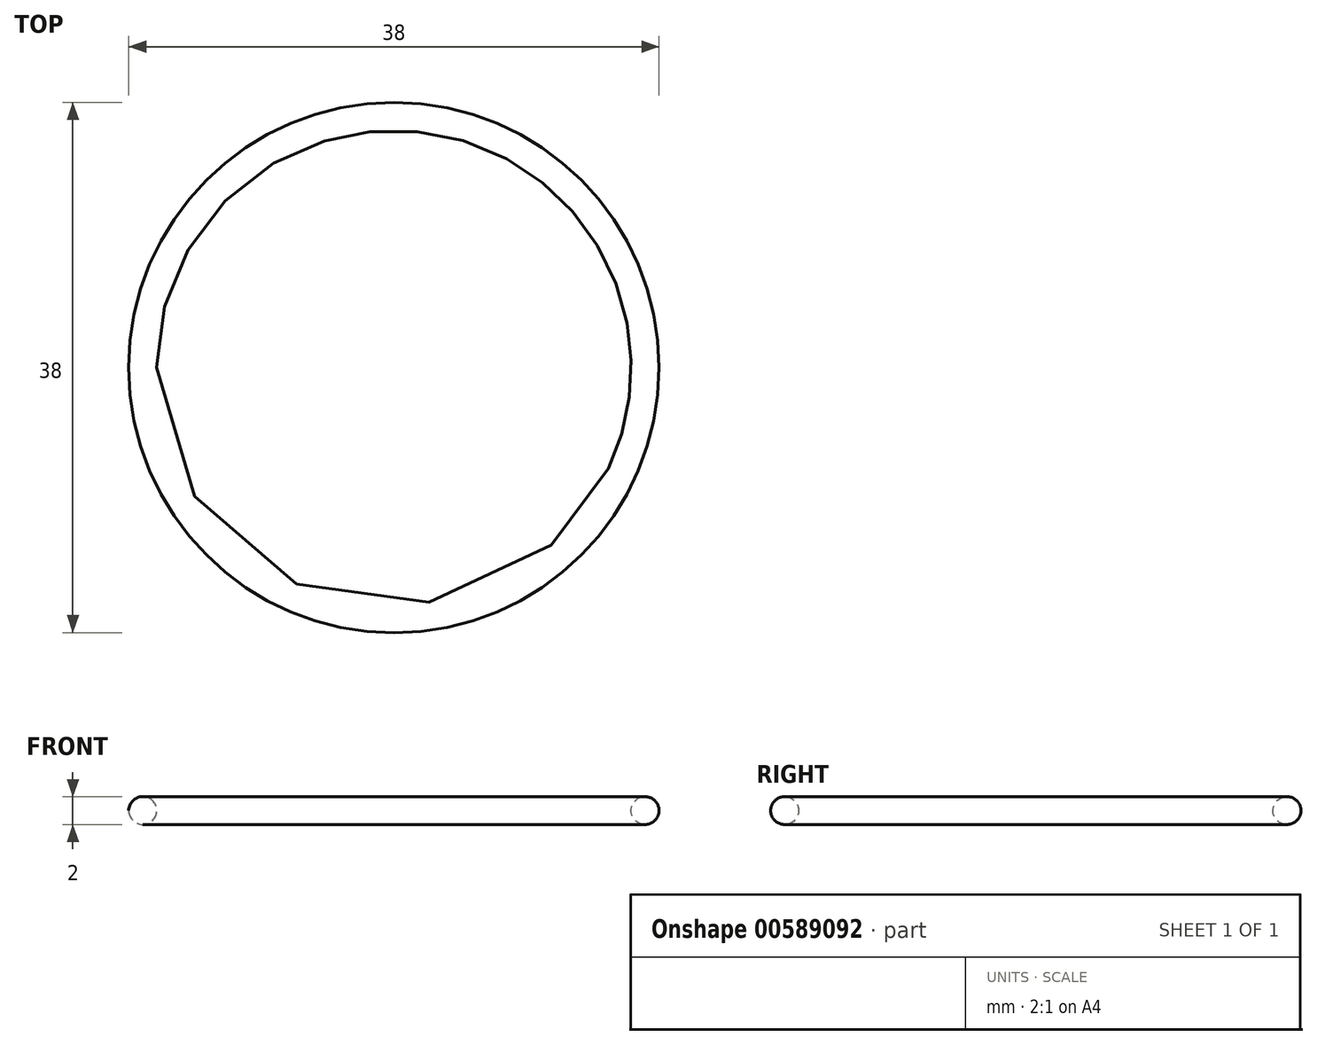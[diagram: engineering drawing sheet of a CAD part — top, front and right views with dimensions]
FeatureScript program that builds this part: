
annotation { "Feature Type Name" : "Feature", "Feature Type Description" : "" }
export const myFeature = defineFeature(function(context is Context, id is Id, definition is map)
    precondition{}
    {
        {
            var Q0;
            Q0=qCreatedBy(makeId("Front.planeOp"),FACE);
            var sketch = newSketch(context, id + "F0", { "sketchPlane" : qUnion([Q0])});
            skCircle(sketch, "E0", {"center": v(-18, 0) * mm, "radius": 1 * mm});
            skLineSegment(sketch, "E1", {"start": v(0, 0) * mm, "end": v(0, 16.38) * mm, "construction": true});
            skSolve(sketch);
        }
        {
            var Q0;
            Q0 = qSketchRegion(id + "F0", true);
            var Q1;
            Q1=sQuery(id+"F0.wireOp",EDGE,"E1");
            revolve(context, id + "F1", {"entities" : qUnion([Q0]), "axis" : qUnion([Q1]), "revolveType" : RevolveType.FULL});
        }
    });
